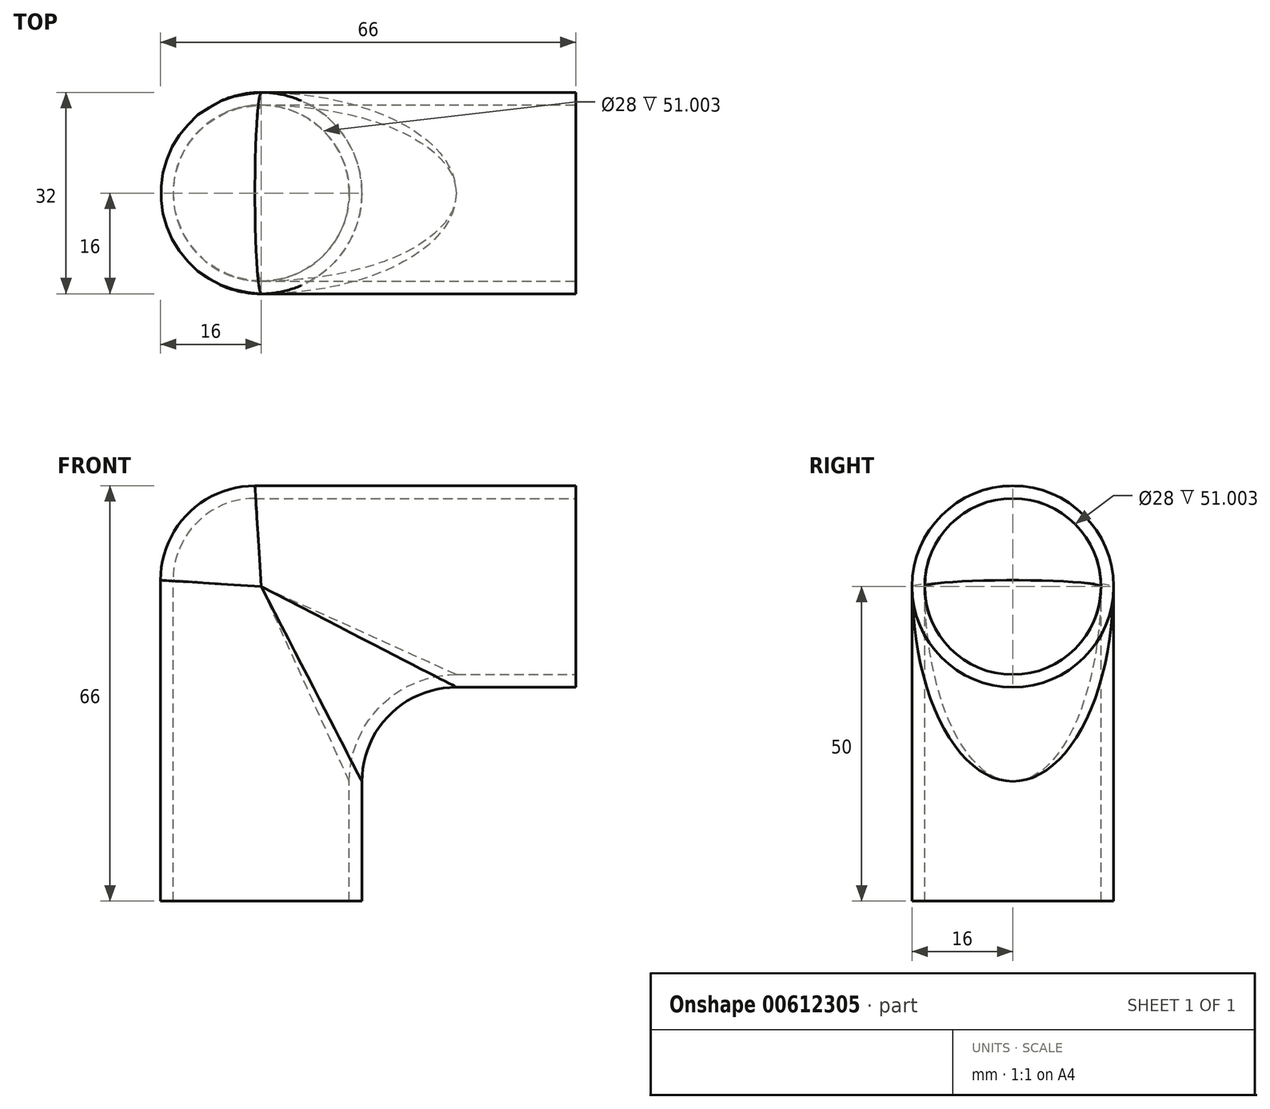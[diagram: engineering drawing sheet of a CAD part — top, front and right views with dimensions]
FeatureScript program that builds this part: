
annotation { "Feature Type Name" : "Feature", "Feature Type Description" : "" }
export const myFeature = defineFeature(function(context is Context, id is Id, definition is map)
    precondition{}
    {
        {
            var Q0;
            Q0=qCreatedBy(makeId("Front.planeOp"),FACE);
            var sketch = newSketch(context, id + "F0", { "sketchPlane" : qUnion([Q0])});
            skLineSegment(sketch, "E0", {"start": v(0, -50) * mm, "end": v(0, 0) * mm});
            skLineSegment(sketch, "E1", {"start": v(0, 0) * mm, "end": v(50, 0) * mm});
            skSolve(sketch);
        }
        {
            var Q0;
            Q0=qCreatedBy(makeId("Right.planeOp"),FACE);
            var sketch = newSketch(context, id + "F1", { "sketchPlane" : qUnion([Q0])});
            skCircle(sketch, "E2", {"center": v(0, 0) * mm, "radius": 16 * mm});
            skSolve(sketch);
        }
        {
            var Q0;
            Q0=makeQuery(id+"F1.imprint","IMPRINT",FACE,{"disambiguationData":[TD([[makeQuery(id+"F1.imprint","IMPRINT",EDGE,{"derivedFrom":sQuery(id+"F1.wireOp",EDGE,"E2")}),1.0]])]});
            var Q1;
            Q1=sQuery(id+"F0.wireOp",EDGE,"E1");
            var Q2;
            Q2=sQuery(id+"F0.wireOp",EDGE,"E0");
            sweep(context, id + "F2", {"profiles" : qUnion([Q0]), "path" : qUnion([Q1, Q2])});
        }
        {
            var Q0;
            Q0=makeQuery(id+"F2.opSweep","MID_CAP_EDGE",EDGE,{"disambiguationData":[OSD([sQuery(id+"F0.wireOp",VERTEX,"E0.end"),sQuery(id+"F1.wireOp",EDGE,"E2")])],"capPos":1.0});
            fillet(context, id + "F3", {"entities" : qUnion([Q0]), "radius" : 15 * mm, "tangentPropagation" : true, "allowEdgeOverflow" : false});
        }
        {
            var Q0;
            Q0=makeQuery(id+"F2.opSweep","CAP_FACE",FACE,{"disambiguationData":[OSD([sQuery(id+"F0.wireOp",VERTEX,"E1.end"),sQuery(id+"F1.wireOp",EDGE,"E2")])],"isStart":false});
            var Q1;
            Q1=makeQuery(id+"F2.opSweep","CAP_FACE",FACE,{"disambiguationData":[OSD([sQuery(id+"F0.wireOp",VERTEX,"E0.start"),sQuery(id+"F1.wireOp",EDGE,"E2")])],"isStart":true});
            shell(context, id + "F4", {"entities" : qUnion([Q0, Q1]), "thickness" : 2 * mm});
        }
    });
